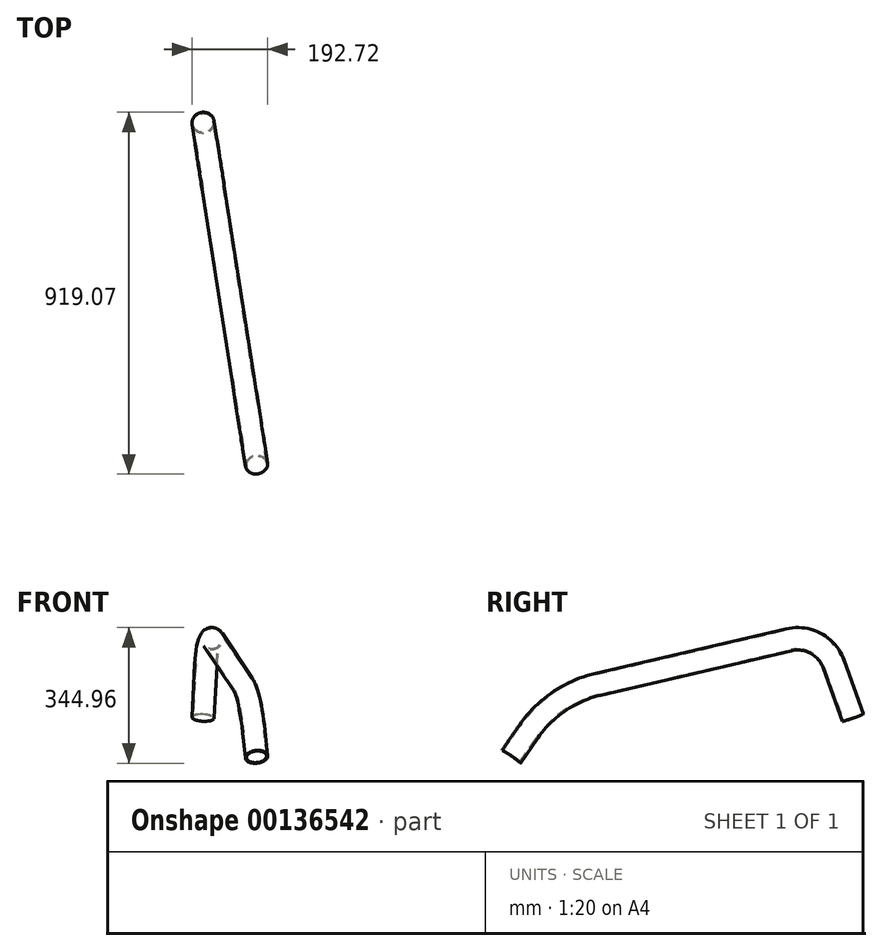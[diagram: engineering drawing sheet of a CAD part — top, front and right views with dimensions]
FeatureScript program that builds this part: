
annotation { "Feature Type Name" : "Feature", "Feature Type Description" : "" }
export const myFeature = defineFeature(function(context is Context, id is Id, definition is map)
    precondition{}
    {
        {
            var Q0;
            Q0=qCreatedBy(makeId("Front.planeOp"),FACE);
            var sketch = newSketch(context, id + "F0", { "sketchPlane" : qUnion([Q0])});
            skLineSegment(sketch, "E0", {"start": v(0, 80.16) * mm, "end": v(0, -80.17) * mm, "construction": true});
            skLineSegment(sketch, "E1", {"start": v(225, 47.48) * mm, "end": v(225, -37.9) * mm});
            skLineSegment(sketch, "E2.MirrorCS", {"start": v(-225, 47.48) * mm, "end": v(-225, -37.9) * mm});
            skSolve(sketch);
        }
        {
            var Q0;
            Q0=qCreatedBy(makeId("Front.planeOp"),FACE);
            cPlane(context, id + "F1", {"entities" : qUnion([Q0]), "cplaneType" : CPlaneType.OFFSET, "offset" : 800 * mm, "width" : 150 * mm, "height" : 150 * mm});
        }
        {
            var Q0;
            Q0=qCreatedBy(id+"F1.planeOp",FACE);
            var sketch = newSketch(context, id + "F2", { "sketchPlane" : qUnion([Q0])});
            skLineSegment(sketch, "E3", {"start": v(0, 288) * mm, "end": v(0, -220) * mm, "construction": true});
            skLineSegment(sketch, "E4", {"start": v(350, 276) * mm, "end": v(350, -248) * mm});
            skLineSegment(sketch, "E5.MirrorCS", {"start": v(-350, 276) * mm, "end": v(-350, -248) * mm});
            skSolve(sketch);
        }
        {
            var Q0;
            Q0=sQuery(id+"F2.wireOp",VERTEX,"E4.start");
            var Q1;
            Q1=sQuery(id+"F2.wireOp",VERTEX,"E4.end");
            var Q2;
            Q2=sQuery(id+"F0.wireOp",VERTEX,"E1.end");
            cPlane(context, id + "F3", {"entities" : qUnion([Q0, Q1, Q2]), "cplaneType" : CPlaneType.THREE_POINT, "offset" : 25 * mm, "width" : 150 * mm, "height" : 150 * mm});
        }
        {
            var Q0;
            Q0=qCreatedBy(id+"F3.planeOp",FACE);
            var sketch = newSketch(context, id + "F4", { "sketchPlane" : qUnion([Q0])});
            skLineSegment(sketch, "E6", {"start": v(224.03, 0) * mm, "end": v(-51.47, 0) * mm, "construction": true});
            skLineSegment(sketch, "E7", {"start": v(844.44, 0) * mm, "end": v(799.72, 63.86) * mm});
            skLineSegment(sketch, "E8", {"start": v(621.46, 184.1) * mm, "end": v(130.58, 297.43) * mm});
            skLineSegment(sketch, "E9", {"start": v(14.11, 234.2) * mm, "end": v(-34.73, 100) * mm});
            skPoint(sketch, "E10.visualSharp", {"position": v(733.67, 158.2) * mm});
            skArc(sketch, "E10.filletArc", {"start": v(799.72, 63.86) * mm, "mid": v(721.73, 140.5) * mm, "end": v(621.46, 184.1) * mm});
            skPoint(sketch, "E11.visualSharp", {"position": v(44.37, 317.33) * mm});
            skArc(sketch, "E11.filletArc", {"start": v(130.58, 297.43) * mm, "mid": v(60.36, 287.88) * mm, "end": v(14.11, 234.2) * mm});
            skSolve(sketch);
        }
        {
            var Q0;
            Q0=sQuery(id+"F4.wireOp",VERTEX,"E7.start");
            var Q1;
            Q1=sQuery(id+"F4.wireOp",EDGE,"E7");
            cPlane(context, id + "F5", {"entities" : qUnion([Q0, Q1]), "cplaneType" : CPlaneType.LINE_POINT, "offset" : 25 * mm, "width" : 150 * mm, "height" : 150 * mm});
        }
        {
            var Q0;
            Q0=qCreatedBy(id+"F5.planeOp",FACE);
            var sketch = newSketch(context, id + "F6", { "sketchPlane" : qUnion([Q0])});
            skCircle(sketch, "E12", {"center": v(308.32, -657.9) * mm, "radius": 28.57 * mm});
            skCircle(sketch, "E13", {"center": v(308.32, -657.9) * mm, "radius": 25.8 * mm});
            skSolve(sketch);
        }
        {
            var Q0;
            Q0 = qSketchRegion(id + "F6", true);
            var Q1;
            Q1 = qConstructionFilter(qBodyType(qCreatedBy(id + "F4" ,EDGE), BodyType.WIRE), ConstructionObject.NO);
            sweep(context, id + "F7", {"profiles" : qUnion([Q0]), "path" : qUnion([Q1])});
        }
    });
